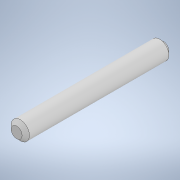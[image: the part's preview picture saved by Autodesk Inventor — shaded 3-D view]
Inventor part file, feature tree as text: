
AUTODESK INVENTOR PART (.ipt)
format: ipt  version: 2022 (Build 260153000, 153)  size: 95,744 bytes
history: native  units: mm
features: extrude x1, chamfer x1, sketch x1
ambient origin geometry x8: Origin, YZ Plane, XZ Plane, XY Plane, X Axis, Y Axis, Z Axis, Center Point
bodies: Solid1 (feature_tree)
feature tree (3):
  extrude  "Extrusion1"  Depth=40.0mm TaperAngle=0.0deg
  chamfer  "Chamfer1"  Distance=2.0mm Angle=45.0deg
  sketch  "Sketch1"  dims[d0=5.0mm d1=40.0mm d2=0.0mm d3=1.0mm d4=2.0mm d5=45.0deg]
